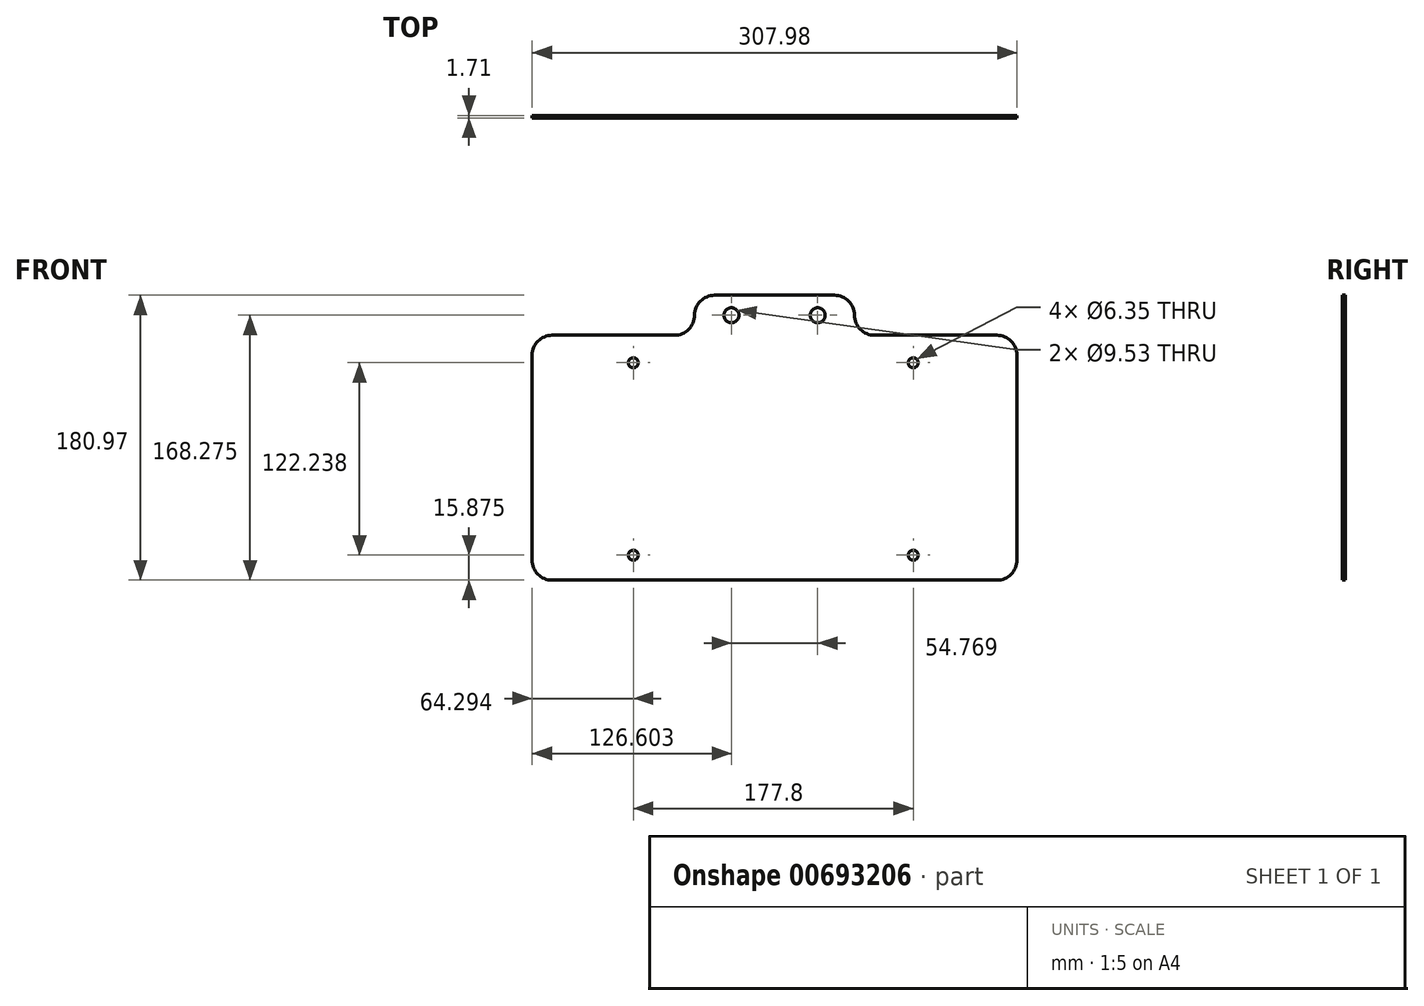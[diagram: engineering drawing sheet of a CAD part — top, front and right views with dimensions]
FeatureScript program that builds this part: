
annotation { "Feature Type Name" : "Feature", "Feature Type Description" : "" }
export const myFeature = defineFeature(function(context is Context, id is Id, definition is map)
    precondition{}
    {
        {
            var Q0;
            Q0=qCreatedBy(makeId("Front.planeOp"),FACE);
            var sketch = newSketch(context, id + "F0", { "sketchPlane" : qUnion([Q0])});
            skLineSegment(sketch, "E0.bottom", {"start": v(12.7, 0) * mm, "end": v(295.28, 0) * mm});
            skLineSegment(sketch, "E0.top", {"start": v(12.7, 155.58) * mm, "end": v(90.49, 155.58) * mm});
            skLineSegment(sketch, "E0.left", {"start": v(0, 12.7) * mm, "end": v(0, 142.88) * mm});
            skLineSegment(sketch, "E0.right", {"start": v(307.98, 12.7) * mm, "end": v(307.98, 142.88) * mm});
            skLineSegment(sketch, "E1.top", {"start": v(115.89, 180.98) * mm, "end": v(192.09, 180.98) * mm});
            skLineSegment(sketch, "E1.left", {"start": v(103.19, 168.28) * mm, "end": v(103.19, 168.28) * mm});
            skLineSegment(sketch, "E1.right", {"start": v(204.79, 168.28) * mm, "end": v(204.79, 168.28) * mm});
            skPoint(sketch, "E2.newPointA", {"position": v(103.19, 142.05) * mm});
            skArc(sketch, "E2.filletArc", {"start": v(90.49, 155.58) * mm, "mid": v(99.47, 159.3) * mm, "end": v(103.19, 168.28) * mm});
            skLineSegment(sketch, "E3", {"start": v(217.49, 155.58) * mm, "end": v(295.28, 155.58) * mm});
            skPoint(sketch, "E4.visualSharp", {"position": v(204.79, 155.58) * mm});
            skArc(sketch, "E4.filletArc", {"start": v(204.79, 168.28) * mm, "mid": v(208.5, 159.3) * mm, "end": v(217.49, 155.58) * mm});
            skCircle(sketch, "E5", {"center": v(126.6, 168.28) * mm, "radius": 4.76 * mm});
            skCircle(sketch, "E6", {"center": v(181.37, 168.28) * mm, "radius": 4.76 * mm});
            skPoint(sketch, "E7.visualSharp", {"position": v(0, 155.58) * mm});
            skArc(sketch, "E7.filletArc", {"start": v(12.7, 155.58) * mm, "mid": v(3.72, 151.86) * mm, "end": v(0, 142.88) * mm});
            skPoint(sketch, "E8.visualSharp", {"position": v(0, 0) * mm});
            skArc(sketch, "E8.filletArc", {"start": v(0, 12.7) * mm, "mid": v(3.72, 3.72) * mm, "end": v(12.7, 0) * mm});
            skPoint(sketch, "E9.visualSharp", {"position": v(307.98, 0) * mm});
            skArc(sketch, "E9.filletArc", {"start": v(295.28, 0) * mm, "mid": v(304.26, 3.72) * mm, "end": v(307.98, 12.7) * mm});
            skPoint(sketch, "E10.visualSharp", {"position": v(307.98, 155.58) * mm});
            skArc(sketch, "E10.filletArc", {"start": v(307.98, 142.88) * mm, "mid": v(304.26, 151.86) * mm, "end": v(295.28, 155.58) * mm});
            skPoint(sketch, "E11.visualSharp", {"position": v(204.79, 180.98) * mm});
            skArc(sketch, "E11.filletArc", {"start": v(204.79, 168.28) * mm, "mid": v(201.07, 177.26) * mm, "end": v(192.09, 180.98) * mm});
            skPoint(sketch, "E12.visualSharp", {"position": v(103.19, 180.98) * mm});
            skArc(sketch, "E12.filletArc", {"start": v(115.89, 180.98) * mm, "mid": v(106.9, 177.26) * mm, "end": v(103.19, 168.28) * mm});
            skCircle(sketch, "E13", {"center": v(64.3, 138.11) * mm, "radius": 3.18 * mm});
            skCircle(sketch, "E14", {"center": v(242.1, 138.11) * mm, "radius": 3.18 * mm});
            skCircle(sketch, "E15", {"center": v(242.1, 15.88) * mm, "radius": 3.18 * mm});
            skCircle(sketch, "E16", {"center": v(64.3, 15.88) * mm, "radius": 3.18 * mm});
            skSolve(sketch);
        }
        {
            var Q0;
            Q0=makeQuery(id+"F0.imprint","IMPRINT",FACE,{"disambiguationData":[TD([[makeQuery(id+"F0.imprint","IMPRINT",EDGE,{"derivedFrom":sQuery(id+"F0.wireOp",EDGE,"E0.bottom")}),1.0]])]});
            extrude(context, id + "F1", {"entities" : qUnion([Q0]), "depth" : 1.71 * mm, "offsetDistance" : 25.4 * mm});
        }
    });
